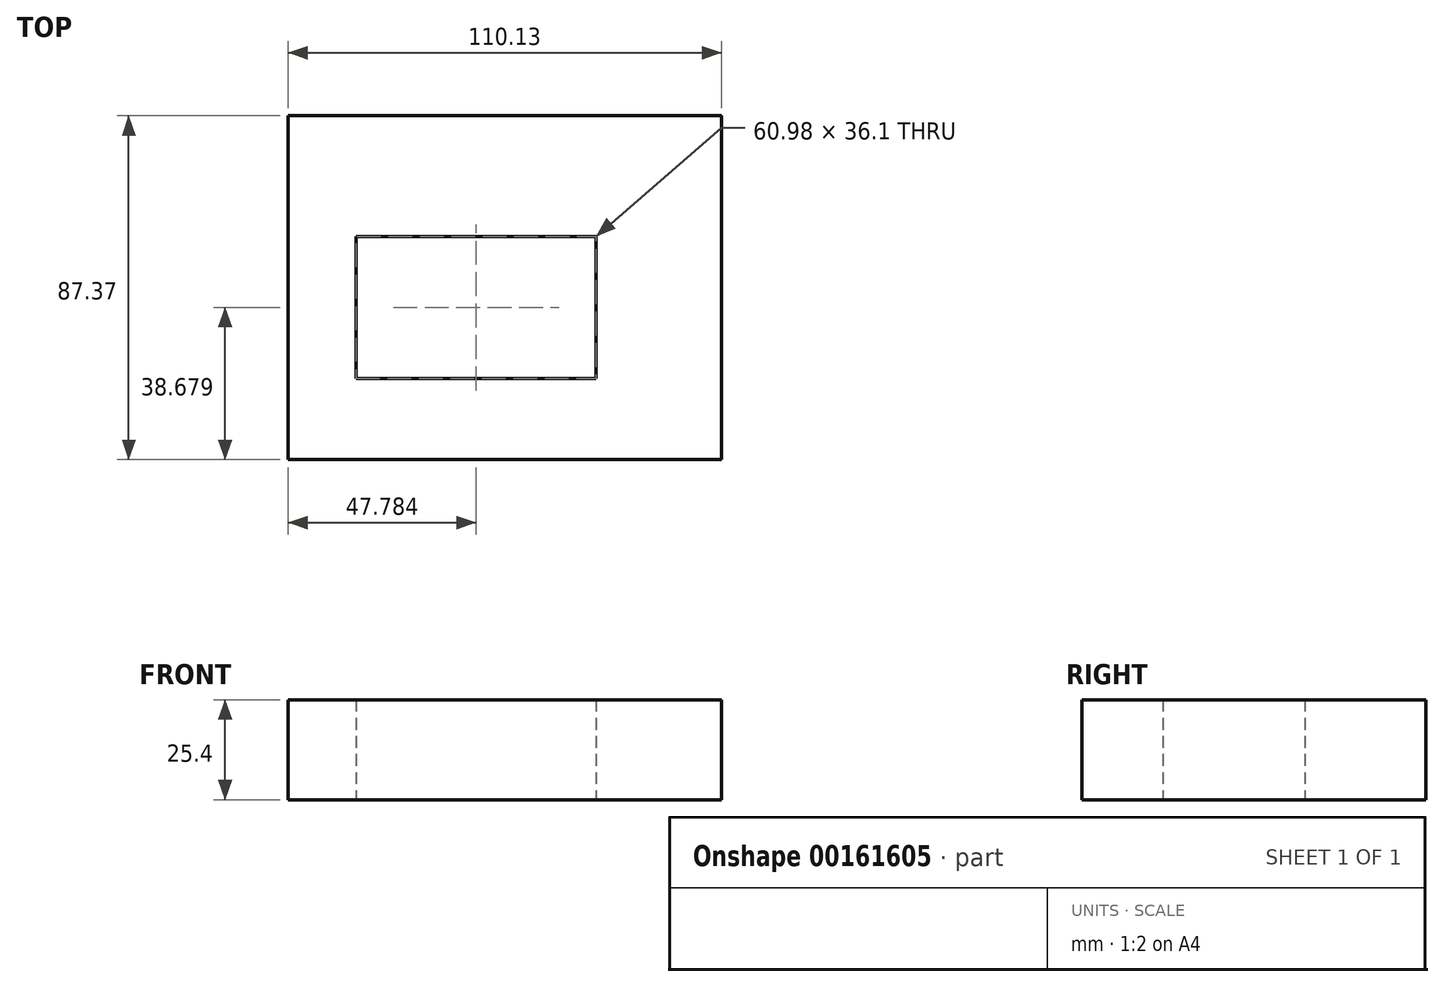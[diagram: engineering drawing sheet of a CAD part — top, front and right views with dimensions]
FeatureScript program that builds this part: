
annotation { "Feature Type Name" : "Feature", "Feature Type Description" : "" }
export const myFeature = defineFeature(function(context is Context, id is Id, definition is map)
    precondition{}
    {
        {
            var Q0;
            Q0=qCreatedBy(makeId("Top.planeOp"),FACE);
            var sketch = newSketch(context, id + "F0", { "sketchPlane" : qUnion([Q0])});
            skLineSegment(sketch, "E0.bottom", {"start": v(-50.97, 45.05) * mm, "end": v(59.16, 45.05) * mm});
            skLineSegment(sketch, "E0.top", {"start": v(-50.97, -42.32) * mm, "end": v(59.16, -42.32) * mm});
            skLineSegment(sketch, "E0.left", {"start": v(-50.97, 45.05) * mm, "end": v(-50.97, -42.32) * mm});
            skLineSegment(sketch, "E0.right", {"start": v(59.16, 45.05) * mm, "end": v(59.16, -42.32) * mm});
            skLineSegment(sketch, "E1.bottom", {"start": v(27, 45.05) * mm, "end": v(-50.97, 45.05) * mm});
            skLineSegment(sketch, "E1.top", {"start": v(27, 14.41) * mm, "end": v(-50.97, 14.41) * mm});
            skLineSegment(sketch, "E1.left", {"start": v(27, 45.05) * mm, "end": v(27, 14.41) * mm});
            skLineSegment(sketch, "E1.right", {"start": v(-50.97, 45.05) * mm, "end": v(-50.97, 14.41) * mm});
            skLineSegment(sketch, "E2.bottom", {"start": v(-33.68, 14.41) * mm, "end": v(27.3, 14.41) * mm});
            skLineSegment(sketch, "E2.top", {"start": v(-33.68, -21.7) * mm, "end": v(27.3, -21.7) * mm});
            skLineSegment(sketch, "E2.left", {"start": v(-33.68, 14.41) * mm, "end": v(-33.68, -21.7) * mm});
            skLineSegment(sketch, "E2.right", {"start": v(27.3, 14.41) * mm, "end": v(27.3, -21.7) * mm});
            skLineSegment(sketch, "E3.bottom", {"start": v(0, 0) * mm, "end": v(23.97, 0) * mm});
            skLineSegment(sketch, "E3.top", {"start": v(0, -21.7) * mm, "end": v(23.97, -21.7) * mm});
            skLineSegment(sketch, "E3.left", {"start": v(0, 0) * mm, "end": v(0, -21.7) * mm});
            skLineSegment(sketch, "E3.right", {"start": v(23.97, 0) * mm, "end": v(23.97, -21.7) * mm});
            skSolve(sketch);
        }
        {
            var Q0;
            Q0 = qSketchRegion(id + "F0", true);
            extrude(context, id + "F1", {"entities" : qUnion([Q0]), "depth" : 25.4 * mm});
        }
        {
            var Q0;
            Q0 = qSketchRegion(id + "F0", true);
            extrude(context, id + "F2", {"entities" : qUnion([Q0]), "operationType" : NewBodyOperationType.ADD, "depth" : 25.4 * mm});
        }
    });
